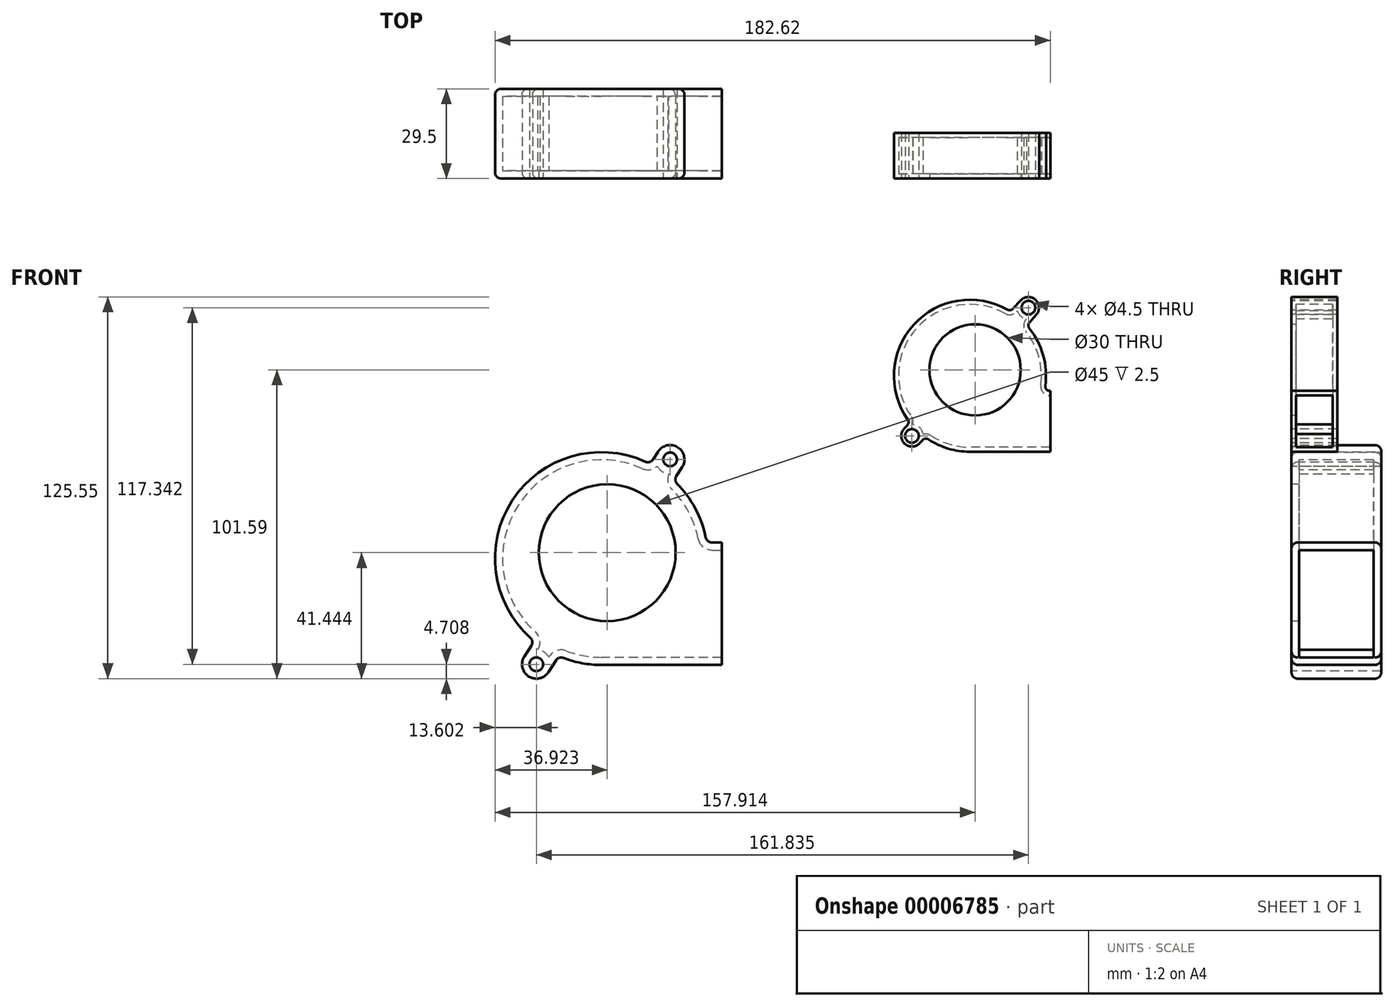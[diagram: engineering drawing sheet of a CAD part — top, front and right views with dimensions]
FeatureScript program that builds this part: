
annotation { "Feature Type Name" : "Feature", "Feature Type Description" : "" }
export const myFeature = defineFeature(function(context is Context, id is Id, definition is map)
    precondition{}
    {
        {
            var Q0;
            Q0=qCreatedBy(makeId("Front.planeOp"),FACE);
            var sketch = newSketch(context, id + "F0", { "sketchPlane" : qUnion([Q0])});
            skArc(sketch, "E0", {"start": v(-86.9, -53.24) * mm, "mid": v(-90.32, -43.7) * mm, "end": v(-96.33, -35.53) * mm});
            skLineSegment(sketch, "E1", {"start": v(-84.95, -54.85) * mm, "end": v(-81.62, -54.85) * mm});
            skLineSegment(sketch, "E2", {"start": v(-81.62, -54.85) * mm, "end": v(-81.62, -95.15) * mm});
            skLineSegment(sketch, "E3", {"start": v(-81.62, -95.15) * mm, "end": v(-121.22, -95.15) * mm});
            skCircle(sketch, "E4", {"center": v(-142.62, -94.94) * mm, "radius": 2.25 * mm});
            skCircle(sketch, "E5", {"center": v(-142.62, -94.94) * mm, "radius": 4.71 * mm});
            skCircle(sketch, "E6", {"center": v(-98.62, -27.53) * mm, "radius": 2.25 * mm});
            skCircle(sketch, "E7", {"center": v(-98.62, -27.53) * mm, "radius": 4.71 * mm});
            skLineSegment(sketch, "E8", {"start": v(-144.23, -88.8) * mm, "end": v(-146.56, -92.37) * mm});
            skLineSegment(sketch, "E9", {"start": v(-138.67, -97.52) * mm, "end": v(-136.12, -93.6) * mm});
            skLineSegment(sketch, "E10", {"start": v(-102.56, -24.96) * mm, "end": v(-104.25, -27.55) * mm});
            skLineSegment(sketch, "E11", {"start": v(-94.67, -30.1) * mm, "end": v(-96.59, -33.04) * mm});
            skArc(sketch, "E12.trimOffspring", {"start": v(-106.75, -28.27) * mm, "mid": v(-150.53, -41.02) * mm, "end": v(-144.57, -86.21) * mm});
            skArc(sketch, "E13.trimOffspring", {"start": v(-133.73, -92.83) * mm, "mid": v(-127.58, -94.56) * mm, "end": v(-121.22, -95.15) * mm});
            skPoint(sketch, "E14.visualSharp", {"position": v(-105.21, -29.02) * mm});
            skArc(sketch, "E14.filletArc", {"start": v(-106.75, -28.27) * mm, "mid": v(-105.37, -28.37) * mm, "end": v(-104.25, -27.55) * mm});
            skPoint(sketch, "E15.visualSharp", {"position": v(-97.49, -34.42) * mm});
            skArc(sketch, "E15.filletArc", {"start": v(-96.59, -33.04) * mm, "mid": v(-96.9, -34.33) * mm, "end": v(-96.33, -35.53) * mm});
            skPoint(sketch, "E16.visualSharp", {"position": v(-86.62, -54.85) * mm});
            skArc(sketch, "E16.filletArc", {"start": v(-86.9, -53.24) * mm, "mid": v(-86.21, -54.4) * mm, "end": v(-84.95, -54.85) * mm});
            skPoint(sketch, "E17.visualSharp", {"position": v(-135.22, -92.22) * mm});
            skArc(sketch, "E17.filletArc", {"start": v(-133.73, -92.83) * mm, "mid": v(-135.06, -92.8) * mm, "end": v(-136.12, -93.6) * mm});
            skPoint(sketch, "E18.visualSharp", {"position": v(-143.27, -87.32) * mm});
            skArc(sketch, "E18.filletArc", {"start": v(-144.23, -88.8) * mm, "mid": v(-143.92, -87.44) * mm, "end": v(-144.57, -86.21) * mm});
            skPoint(sketch, "E19", {"position": v(-119.62, -59.13) * mm});
            skLineSegment(sketch, "E20", {"start": v(-144.23, -88.8) * mm, "end": v(-104.25, -27.55) * mm, "construction": true});
            skCircle(sketch, "E21", {"center": v(-119.3, -58.2) * mm, "radius": 22.5 * mm});
            skSolve(sketch);
        }
        {
            var Q0;
            Q0=makeQuery(id+"F0.imprint","IMPRINT",FACE,{"disambiguationData":[TD([[makeQuery(id+"F0.imprint","IMPRINT",EDGE,{"derivedFrom":sQuery(id+"F0.wireOp",EDGE,"E0")}),1.0]])]});
            var Q1;
            Q1=makeQuery(id+"F0.imprint","IMPRINT",FACE,{"disambiguationData":[TD([[makeQuery(id+"F0.imprint","IMPRINT",EDGE,{"derivedFrom":sQuery(id+"F0.wireOp",EDGE,"E21")}),1.0]])]});
            var Q2;
            Q2=makeQuery(id+"F0.imprint","IMPRINT",FACE,{"disambiguationData":[TD([[makeQuery(id+"F0.imprint","IMPRINT",EDGE,{"derivedFrom":sQuery(id+"F0.wireOp",EDGE,"E6")}),-1.0]])]});
            var Q3;
            Q3=makeQuery(id+"F0.imprint","IMPRINT",FACE,{"disambiguationData":[TD([[makeQuery(id+"F0.imprint","IMPRINT",EDGE,{"derivedFrom":sQuery(id+"F0.wireOp",EDGE,"E4")}),-1.0]])]});
            extrude(context, id + "F1", {"entities" : qUnion([Q0, Q1, Q2, Q3]), "oppositeDirection" : true, "depth" : 29.5 * mm, "offsetDistance" : 25 * mm});
        }
        {
            var Q0;
            Q0=makeQuery(id+"F1.opExtrude","SWEPT_FACE",FACE,{"disambiguationData":[OSD([sQuery(id+"F0.wireOp",EDGE,"E2")])]});
            shell(context, id + "F2", {"entities" : qUnion([Q0]), "thickness" : 2.5 * mm});
        }
        {
            var Q0;
            Q0=makeQuery(id+"F0.imprint","IMPRINT",FACE,{"disambiguationData":[TD([[makeQuery(id+"F0.imprint","IMPRINT",EDGE,{"derivedFrom":sQuery(id+"F0.wireOp",EDGE,"E21")}),1.0]])]});
            extrude(context, id + "F3", {"entities" : qUnion([Q0]), "operationType" : NewBodyOperationType.REMOVE, "oppositeDirection" : true, "depth" : 25 * mm, "offsetDistance" : 25 * mm});
        }
        {
            var Q0;
            Q0=makeQuery(id+"F1.opExtrude","CAP_EDGE",EDGE,{"disambiguationData":[OSD([sQuery(id+"F0.wireOp",EDGE,"E3")])],"isStart":true});
            var Q1;
            Q1=makeQuery(id+"F1.opExtrude","CAP_EDGE",EDGE,{"disambiguationData":[OSD([sQuery(id+"F0.wireOp",EDGE,"E3")])],"isStart":false});
            fillet(context, id + "F4", {"entities" : qUnion([Q0, Q1]), "radius" : 2 * mm, "tangentPropagation" : true, "allowEdgeOverflow" : false});
        }
        {
            var Q0;
            Q0=qCreatedBy(makeId("Front.planeOp"),FACE);
            var sketch = newSketch(context, id + "F5", { "sketchPlane" : qUnion([Q0])});
            skArc(sketch, "E22", {"start": v(24.78, -3.3) * mm, "mid": v(24.08, 6.7) * mm, "end": v(19.5, 15.63) * mm});
            skLineSegment(sketch, "E23", {"start": v(26.27, -5) * mm, "end": v(26.4, -5) * mm});
            skLineSegment(sketch, "E24", {"start": v(26.4, -5) * mm, "end": v(26.4, -25) * mm});
            skLineSegment(sketch, "E25", {"start": v(26.4, -25) * mm, "end": v(0, -25) * mm});
            skCircle(sketch, "E26", {"center": v(-19.1, -19.8) * mm, "radius": 2.25 * mm});
            skCircle(sketch, "E27", {"center": v(-19.1, -19.8) * mm, "radius": 3.5 * mm});
            skCircle(sketch, "E28", {"center": v(19.22, 22.4) * mm, "radius": 2.25 * mm});
            skCircle(sketch, "E29", {"center": v(19.22, 22.4) * mm, "radius": 3.5 * mm});
            skLineSegment(sketch, "E30", {"start": v(-20.58, -16.23) * mm, "end": v(-21.7, -17.45) * mm});
            skLineSegment(sketch, "E31", {"start": v(-16.5, -22.15) * mm, "end": v(-15.62, -21.17) * mm});
            skLineSegment(sketch, "E32", {"start": v(16.63, 24.75) * mm, "end": v(14.17, 22.05) * mm});
            skLineSegment(sketch, "E33", {"start": v(21.8, 20.05) * mm, "end": v(19.57, 17.58) * mm});
            skArc(sketch, "E34.trimOffspring", {"start": v(12.32, 21.75) * mm, "mid": v(-18.5, 16.8) * mm, "end": v(-20.47, -14.36) * mm});
            skArc(sketch, "E35.trimOffspring", {"start": v(-13.68, -20.92) * mm, "mid": v(-7.14, -23.96) * mm, "end": v(0, -25) * mm});
            skPoint(sketch, "E36.visualSharp", {"position": v(13.35, 21.14) * mm});
            skArc(sketch, "E36.filletArc", {"start": v(12.32, 21.75) * mm, "mid": v(13.3, 21.58) * mm, "end": v(14.17, 22.05) * mm});
            skPoint(sketch, "E37.visualSharp", {"position": v(18.69, 16.6) * mm});
            skArc(sketch, "E37.filletArc", {"start": v(19.57, 17.58) * mm, "mid": v(19.18, 16.62) * mm, "end": v(19.5, 15.63) * mm});
            skPoint(sketch, "E38.visualSharp", {"position": v(24.5, -5) * mm});
            skArc(sketch, "E38.filletArc", {"start": v(24.78, -3.3) * mm, "mid": v(25.14, -4.49) * mm, "end": v(26.27, -5) * mm});
            skPoint(sketch, "E39.visualSharp", {"position": v(-14.73, -20.2) * mm});
            skArc(sketch, "E39.filletArc", {"start": v(-13.68, -20.92) * mm, "mid": v(-14.7, -20.69) * mm, "end": v(-15.62, -21.17) * mm});
            skPoint(sketch, "E40.visualSharp", {"position": v(-19.76, -15.32) * mm});
            skArc(sketch, "E40.filletArc", {"start": v(-20.58, -16.23) * mm, "mid": v(-20.2, -15.31) * mm, "end": v(-20.47, -14.36) * mm});
            skPoint(sketch, "E41", {"position": v(0, -7.63) * mm});
            skLineSegment(sketch, "E42", {"start": v(-20.58, -16.23) * mm, "end": v(14.17, 22.05) * mm, "construction": true});
            skCircle(sketch, "E43", {"center": v(1.7, 1.94) * mm, "radius": 15 * mm});
            skSolve(sketch);
        }
        {
            var Q0;
            Q0=makeQuery(id+"F5.imprint","IMPRINT",FACE,{"disambiguationData":[TD([[makeQuery(id+"F5.imprint","IMPRINT",EDGE,{"derivedFrom":sQuery(id+"F5.wireOp",EDGE,"E22")}),1.0]])]});
            var Q1;
            Q1=makeQuery(id+"F5.imprint","IMPRINT",FACE,{"disambiguationData":[TD([[makeQuery(id+"F5.imprint","IMPRINT",EDGE,{"derivedFrom":sQuery(id+"F5.wireOp",EDGE,"E28")}),-1.0]])]});
            var Q2;
            Q2=makeQuery(id+"F5.imprint","IMPRINT",FACE,{"disambiguationData":[TD([[makeQuery(id+"F5.imprint","IMPRINT",EDGE,{"derivedFrom":sQuery(id+"F5.wireOp",EDGE,"E26")}),-1.0]])]});
            var Q3;
            Q3=makeQuery(id+"F5.imprint","IMPRINT",FACE,{"disambiguationData":[TD([[makeQuery(id+"F5.imprint","IMPRINT",EDGE,{"derivedFrom":sQuery(id+"F5.wireOp",EDGE,"E43")}),1.0]])]});
            extrude(context, id + "F6", {"entities" : qUnion([Q0, Q1, Q2, Q3]), "oppositeDirection" : true, "depth" : 15 * mm, "offsetDistance" : 25 * mm});
        }
        {
            var Q0;
            Q0=makeQuery(id+"F6.opExtrude","SWEPT_FACE",FACE,{"disambiguationData":[OSD([sQuery(id+"F5.wireOp",EDGE,"E24")])]});
            shell(context, id + "F7", {"entities" : qUnion([Q0]), "thickness" : 1.5 * mm});
        }
        {
            var Q0;
            Q0=makeQuery(id+"F5.imprint","IMPRINT",FACE,{"disambiguationData":[TD([[makeQuery(id+"F5.imprint","IMPRINT",EDGE,{"derivedFrom":sQuery(id+"F5.wireOp",EDGE,"E43")}),1.0]])]});
            extrude(context, id + "F8", {"entities" : qUnion([Q0]), "operationType" : NewBodyOperationType.REMOVE, "oppositeDirection" : true, "depth" : 10 * mm, "offsetDistance" : 25 * mm});
        }
    });
